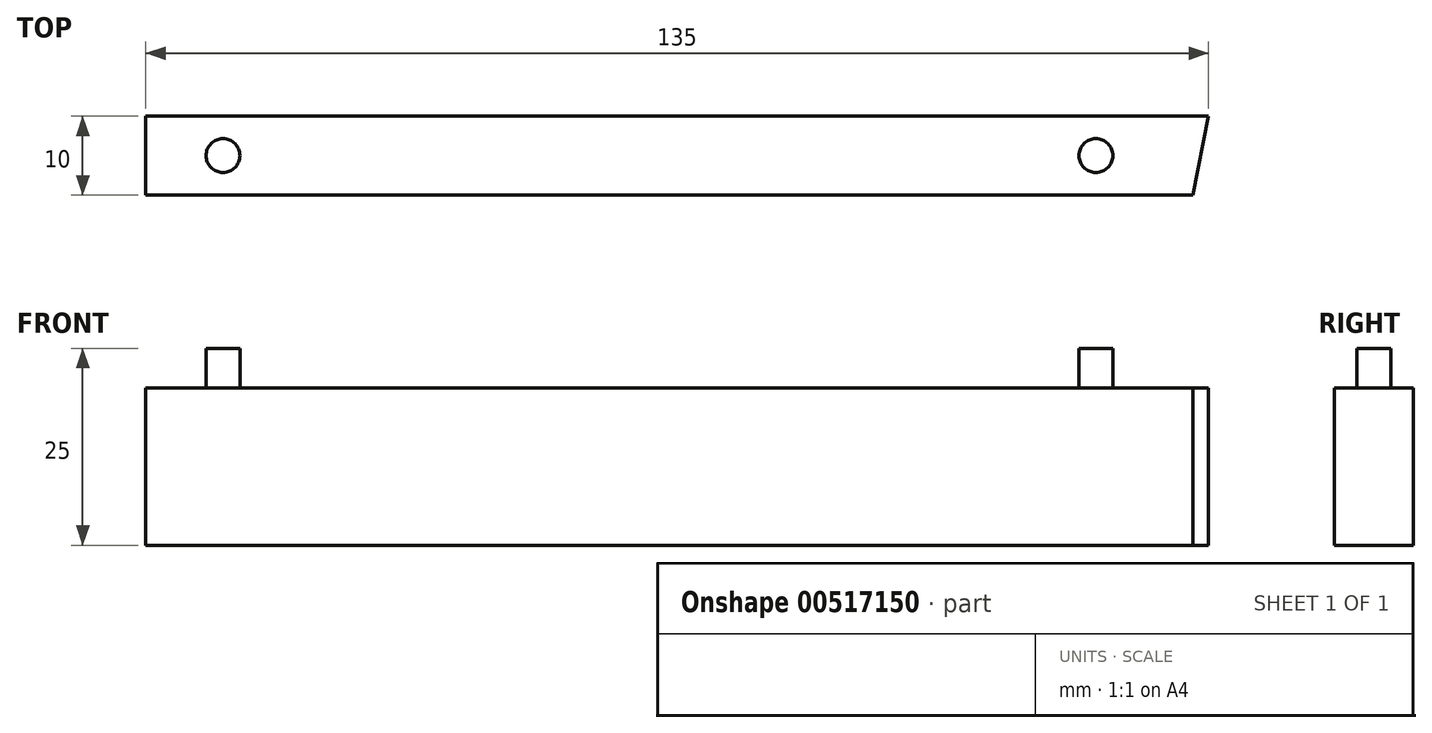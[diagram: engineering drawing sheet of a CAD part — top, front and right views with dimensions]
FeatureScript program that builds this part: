
annotation { "Feature Type Name" : "Feature", "Feature Type Description" : "" }
export const myFeature = defineFeature(function(context is Context, id is Id, definition is map)
    precondition{}
    {
        {
            var Q0;
            Q0=qCreatedBy(makeId("Top.planeOp"),FACE);
            var sketch = newSketch(context, id + "F0", { "sketchPlane" : qUnion([Q0])});
            skLineSegment(sketch, "E0", {"start": v(-67.28, 44.73) * mm, "end": v(-67.28, 34.73) * mm});
            skLineSegment(sketch, "E1", {"start": v(-67.28, 44.73) * mm, "end": v(67.72, 44.73) * mm});
            skLineSegment(sketch, "E2", {"start": v(67.72, 44.73) * mm, "end": v(65.72, 34.73) * mm});
            skLineSegment(sketch, "E3", {"start": v(65.72, 34.73) * mm, "end": v(-67.28, 34.73) * mm});
            skSolve(sketch);
        }
        {
            var Q0;
            Q0=makeQuery(id+"F0.imprint","IMPRINT",FACE,{"disambiguationData":[TD([[makeQuery(id+"F0.imprint","IMPRINT",EDGE,{"derivedFrom":sQuery(id+"F0.wireOp",EDGE,"E0")}),1.0]])]});
            extrude(context, id + "F1", {"entities" : qUnion([Q0]), "depth" : 20 * mm, "offsetDistance" : 25 * mm});
        }
        {
            var Q0;
            Q0=makeQuery(id+"F1.opExtrude","CAP_FACE",FACE,{"disambiguationData":[OSD([sQuery(id+"F0.wireOp",EDGE,"E0"),sQuery(id+"F0.wireOp",EDGE,"E1"),sQuery(id+"F0.wireOp",EDGE,"E2"),sQuery(id+"F0.wireOp",EDGE,"E3")])],"isStart":false});
            var sketch = newSketch(context, id + "F2", { "sketchPlane" : qUnion([Q0])});
            skCircle(sketch, "E4", {"center": v(-57.48, 39.73) * mm, "radius": 2.15 * mm});
            skCircle(sketch, "E5", {"center": v(53.4, 39.73) * mm, "radius": 2.15 * mm});
            skSolve(sketch);
        }
        {
            var Q0;
            Q0=makeQuery(id+"F2.imprint","IMPRINT",FACE,{"disambiguationData":[TD([[makeQuery(id+"F2.imprint","IMPRINT",EDGE,{"derivedFrom":sQuery(id+"F2.wireOp",EDGE,"E4")}),1.0]])]});
            var Q1;
            Q1=makeQuery(id+"F2.imprint","IMPRINT",FACE,{"disambiguationData":[TD([[makeQuery(id+"F2.imprint","IMPRINT",EDGE,{"derivedFrom":sQuery(id+"F2.wireOp",EDGE,"E5")}),1.0]])]});
            extrude(context, id + "F3", {"entities" : qUnion([Q0, Q1]), "operationType" : NewBodyOperationType.ADD, "depth" : 5 * mm, "offsetDistance" : 25 * mm});
        }
    });
